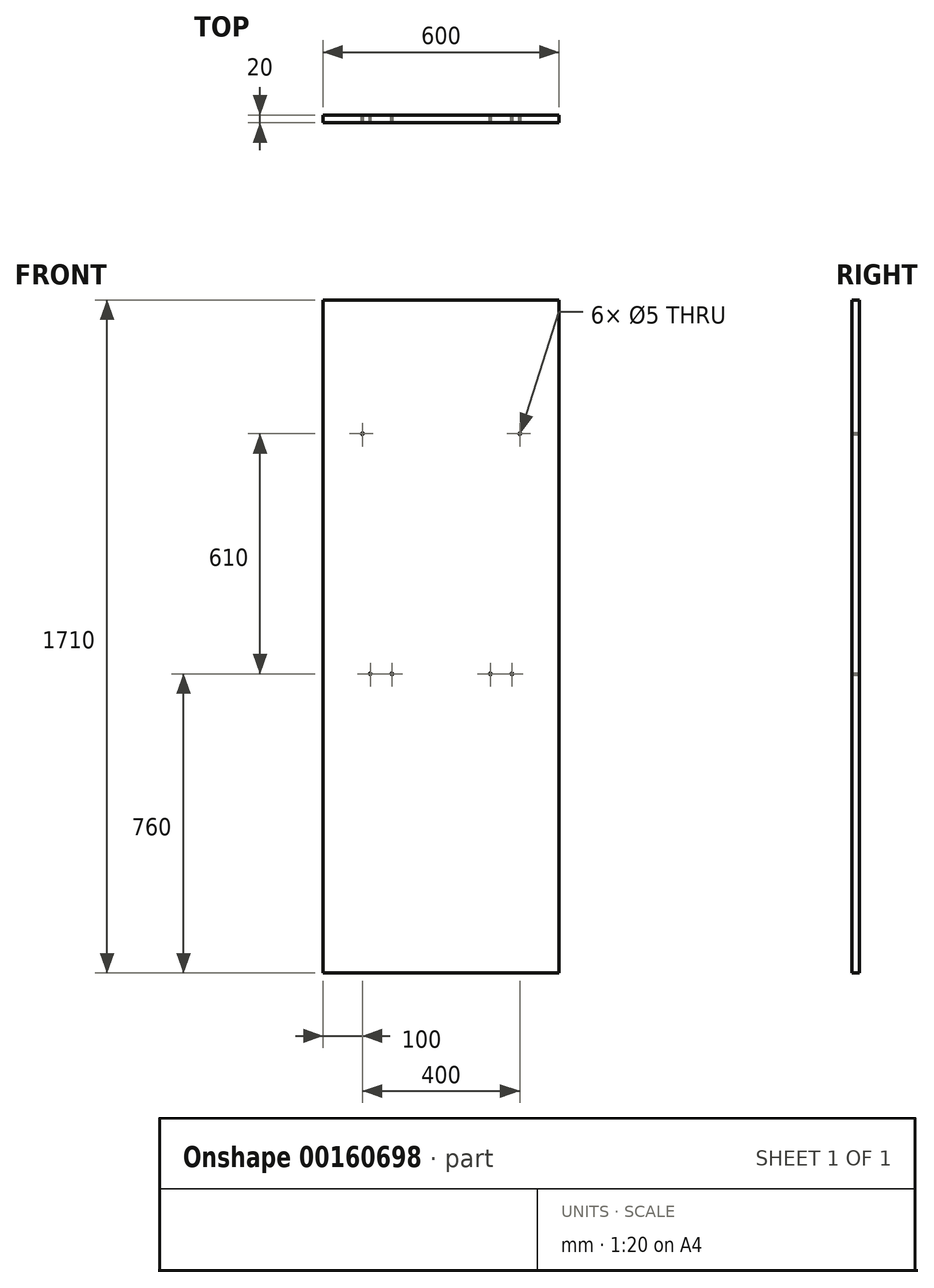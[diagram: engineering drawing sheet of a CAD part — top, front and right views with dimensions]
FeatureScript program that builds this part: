
annotation { "Feature Type Name" : "Feature", "Feature Type Description" : "" }
export const myFeature = defineFeature(function(context is Context, id is Id, definition is map)
    precondition{}
    {
        {
            var Q0;
            Q0=qCreatedBy(makeId("Front.planeOp"),FACE);
            var sketch = newSketch(context, id + "F0", { "sketchPlane" : qUnion([Q0])});
            skLineSegment(sketch, "E0.bottom", {"start": v(-300, 855) * mm, "end": v(300, 855) * mm});
            skLineSegment(sketch, "E0.top", {"start": v(-300, -855) * mm, "end": v(300, -855) * mm});
            skLineSegment(sketch, "E0.left", {"start": v(-300, 855) * mm, "end": v(-300, -855) * mm});
            skLineSegment(sketch, "E0.right", {"start": v(300, 855) * mm, "end": v(300, -855) * mm});
            skLineSegment(sketch, "E1", {"start": v(-518.8, -95) * mm, "end": v(538.7, -95) * mm, "construction": true});
            skCircle(sketch, "E2", {"center": v(-180, -95) * mm, "radius": 2.5 * mm});
            skCircle(sketch, "E3", {"center": v(-125, -95) * mm, "radius": 2.5 * mm});
            skCircle(sketch, "E4.MirrorC", {"center": v(125, -95) * mm, "radius": 2.5 * mm});
            skCircle(sketch, "E5.MirrorC", {"center": v(180, -95) * mm, "radius": 2.5 * mm});
            skLineSegment(sketch, "E6", {"start": v(-365.26, 515) * mm, "end": v(364.91, 515) * mm, "construction": true});
            skCircle(sketch, "E7", {"center": v(-200, 515) * mm, "radius": 2.5 * mm});
            skCircle(sketch, "E8.MirrorC", {"center": v(200, 515) * mm, "radius": 2.5 * mm});
            skSolve(sketch);
        }
        {
            var Q0;
            Q0=makeQuery(id+"F0.imprint","IMPRINT",FACE,{"disambiguationData":[TD([[makeQuery(id+"F0.imprint","IMPRINT",EDGE,{"derivedFrom":sQuery(id+"F0.wireOp",EDGE,"E0.bottom")}),-1.0]])]});
            extrude(context, id + "F1", {"entities" : qUnion([Q0]), "depth" : 20 * mm});
        }
    });
